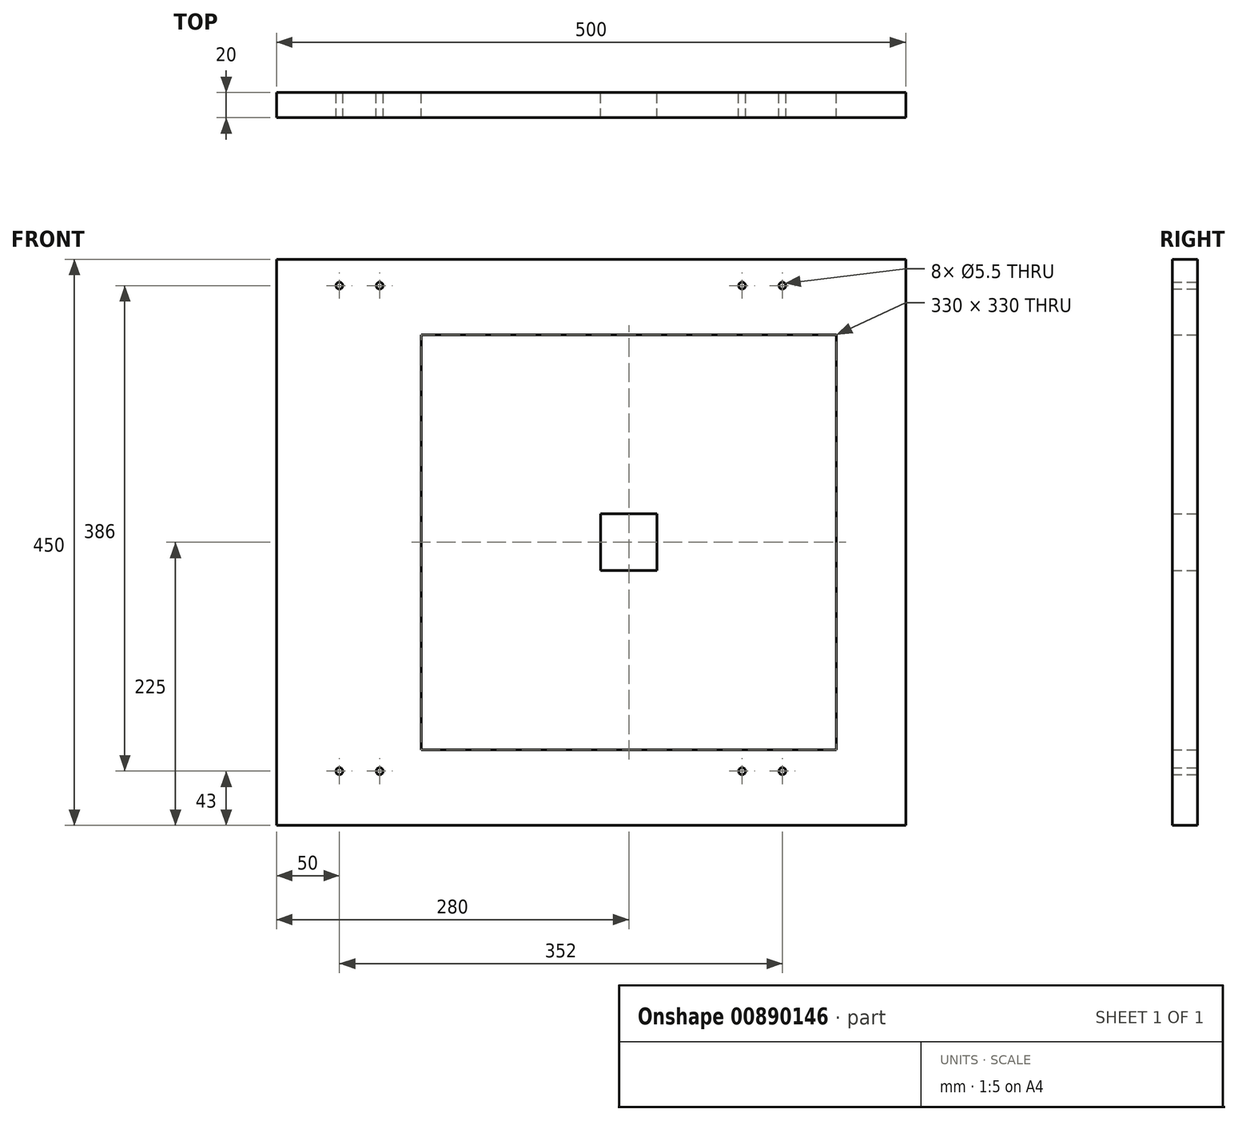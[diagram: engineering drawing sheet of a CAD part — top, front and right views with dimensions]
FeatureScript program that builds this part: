
annotation { "Feature Type Name" : "Feature", "Feature Type Description" : "" }
export const myFeature = defineFeature(function(context is Context, id is Id, definition is map)
    precondition{}
    {
        {
            var Q0;
            Q0=qCreatedBy(makeId("Front.planeOp"),FACE);
            var sketch = newSketch(context, id + "F0", { "sketchPlane" : qUnion([Q0])});
            skPoint(sketch, "E0.middle", {"position": v(0, 0) * mm});
            skCircle(sketch, "E1", {"center": v(-230, 204) * mm, "radius": 2.75 * mm});
            skCircle(sketch, "E2", {"center": v(-198, 204) * mm, "radius": 2.75 * mm});
            skCircle(sketch, "E3", {"center": v(90, 204) * mm, "radius": 2.75 * mm});
            skCircle(sketch, "E4", {"center": v(122, 204) * mm, "radius": 2.75 * mm});
            skCircle(sketch, "E5", {"center": v(-230, -182) * mm, "radius": 2.75 * mm});
            skCircle(sketch, "E6", {"center": v(-198, -182) * mm, "radius": 2.75 * mm});
            skCircle(sketch, "E7", {"center": v(90, -182) * mm, "radius": 2.75 * mm});
            skCircle(sketch, "E8", {"center": v(122, -182) * mm, "radius": 2.75 * mm});
            skLineSegment(sketch, "E9.bottom", {"start": v(-165, 165) * mm, "end": v(165, 165) * mm});
            skLineSegment(sketch, "E9.top", {"start": v(-165, -165) * mm, "end": v(165, -165) * mm});
            skLineSegment(sketch, "E9.left", {"start": v(-165, 165) * mm, "end": v(-165, -165) * mm});
            skLineSegment(sketch, "E9.right", {"start": v(165, 165) * mm, "end": v(165, -165) * mm});
            skLineSegment(sketch, "E10.bottom", {"start": v(-22.5, 165) * mm, "end": v(22.5, 165) * mm});
            skLineSegment(sketch, "E10.top", {"start": v(-22.5, -165) * mm, "end": v(22.5, -165) * mm});
            skLineSegment(sketch, "E10.left", {"start": v(-22.5, 165) * mm, "end": v(-22.5, -165) * mm});
            skLineSegment(sketch, "E10.right", {"start": v(22.5, 165) * mm, "end": v(22.5, -165) * mm});
            skLineSegment(sketch, "E11.bottom", {"start": v(-165, 22.5) * mm, "end": v(165, 22.5) * mm});
            skLineSegment(sketch, "E11.top", {"start": v(-165, -22.5) * mm, "end": v(165, -22.5) * mm});
            skLineSegment(sketch, "E11.left", {"start": v(-165, 22.5) * mm, "end": v(-165, -22.5) * mm});
            skLineSegment(sketch, "E11.right", {"start": v(165, 22.5) * mm, "end": v(165, -22.5) * mm});
            skLineSegment(sketch, "E12.bottom", {"start": v(-280, 225) * mm, "end": v(220, 225) * mm});
            skLineSegment(sketch, "E12.top", {"start": v(-280, -225) * mm, "end": v(220, -225) * mm});
            skLineSegment(sketch, "E12.left", {"start": v(-280, 225) * mm, "end": v(-280, -225) * mm});
            skLineSegment(sketch, "E12.right", {"start": v(220, 225) * mm, "end": v(220, -225) * mm});
            skSolve(sketch);
        }
        {
            var Q0;
            Q0=qSketchRegion(id+"F0",true);
            var Q1;
            {var subQ0=sQuery(id+"F0.wireOp",EDGE,"E10.bottom");Q1=makeQuery(id+"F0.imprint","IMPRINT",FACE,{"disambiguationData":[TD([[makeQuery(id+"F0.imprint","IMPRINT",EDGE,{"derivedFrom":subQ0}),-1.0]])]});}
            var Q2;
            {var subQ5=sQuery(id+"F0.wireOp",EDGE,"E11.left");Q2=makeQuery(id+"F0.imprint","IMPRINT",FACE,{"disambiguationData":[TD([[makeQuery(id+"F0.imprint","IMPRINT",EDGE,{"derivedFrom":subQ5}),1.0]])]});}
            var Q3;
            {var subQ0=sQuery(id+"F0.wireOp",EDGE,"E10.top");Q3=makeQuery(id+"F0.imprint","IMPRINT",FACE,{"disambiguationData":[TD([[makeQuery(id+"F0.imprint","IMPRINT",EDGE,{"derivedFrom":subQ0}),1.0]])]});}
            var Q4;
            {var subQ5=sQuery(id+"F0.wireOp",EDGE,"E11.right");Q4=makeQuery(id+"F0.imprint","IMPRINT",FACE,{"disambiguationData":[TD([[makeQuery(id+"F0.imprint","IMPRINT",EDGE,{"derivedFrom":subQ5}),-1.0]])]});}
            var Q5;
            {var subQ0=sQuery(id+"F0.wireOp",EDGE,"E11.bottom");var subQ1=sQuery(id+"F0.wireOp",EDGE,"E10.left");var subQ2=makeQuery(id+"F0.imprint","INTERSECT",VERTEX,{"derivedFrom":[subQ1,subQ0]});Q5=makeQuery(id+"F0.imprint","IMPRINT",FACE,{"disambiguationData":[TD([[makeQuery(id+"F0.imprint","IMPRINT",EDGE,{"disambiguationData":[TD([[subQ2,-1.0]])],"derivedFrom":subQ1}),1.0]])]});}
            extrude(context, id + "F1", {"entities" : qUnion([Q0, Q1, Q2, Q3, Q4, Q5]), "depth" : 20 * mm, "offsetDistance" : 25 * mm});
        }
    });
